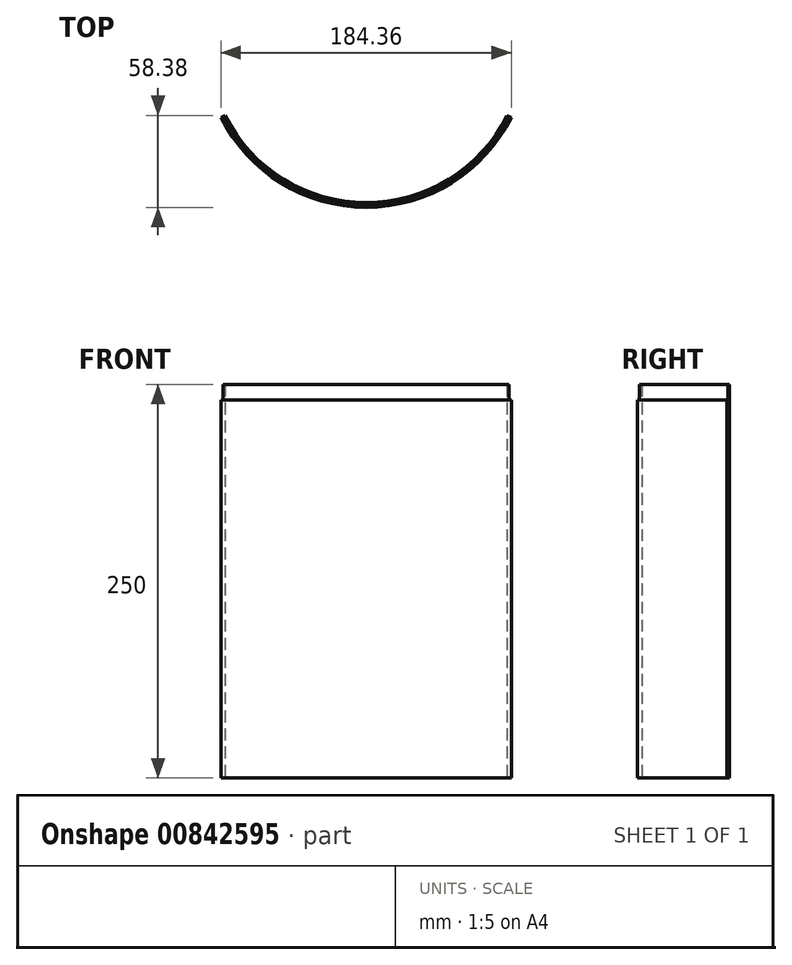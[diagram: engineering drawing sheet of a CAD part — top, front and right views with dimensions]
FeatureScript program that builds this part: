
annotation { "Feature Type Name" : "Feature", "Feature Type Description" : "" }
export const myFeature = defineFeature(function(context is Context, id is Id, definition is map)
    precondition{}
    {
        {
            var Q0;
            Q0=qCreatedBy(makeId("Top.planeOp"),FACE);
            var sketch = newSketch(context, id + "F0", { "sketchPlane" : qUnion([Q0])});
            skArc(sketch, "E0", {"start": v(-92.18, -45.96) * mm, "mid": v(0, -103) * mm, "end": v(92.18, -45.96) * mm});
            skArc(sketch, "E1", {"start": v(-89.5, -44.62) * mm, "mid": v(0, -100) * mm, "end": v(89.5, -44.62) * mm});
            skLineSegment(sketch, "E2", {"start": v(-89.5, -44.62) * mm, "end": v(-92.18, -45.96) * mm});
            skLineSegment(sketch, "E3", {"start": v(89.5, -44.62) * mm, "end": v(92.18, -45.96) * mm});
            skSolve(sketch);
        }
        {
            var Q0;
            Q0 = qSketchRegion(id + "F0", true);
            extrude(context, id + "F1", {"entities" : qUnion([Q0]), "depth" : 250 * mm, "offsetDistance" : 25 * mm});
        }
        {
            var Q0;
            Q0=makeQuery(id+"F1.opExtrude","CAP_FACE",FACE,{"disambiguationData":[OSD([sQuery(id+"F0.wireOp",EDGE,"E0"),sQuery(id+"F0.wireOp",EDGE,"E1"),sQuery(id+"F0.wireOp",EDGE,"E2"),sQuery(id+"F0.wireOp",EDGE,"E3")])],"isStart":false});
            var sketch = newSketch(context, id + "F2", { "sketchPlane" : qUnion([Q0])});
            skCircle(sketch, "E4", {"center": v(0, 0) * mm, "radius": 101.5 * mm});
            skCircle(sketch, "E5", {"center": v(0, 0) * mm, "radius": 103 * mm});
            skSolve(sketch);
        }
        {
            var Q0;
            Q0 = qSketchRegion(id + "F2", true);
            extrude(context, id + "F3", {"entities" : qUnion([Q0]), "operationType" : NewBodyOperationType.REMOVE, "oppositeDirection" : true, "depth" : 10 * mm, "offsetDistance" : 25 * mm});
        }
    });
